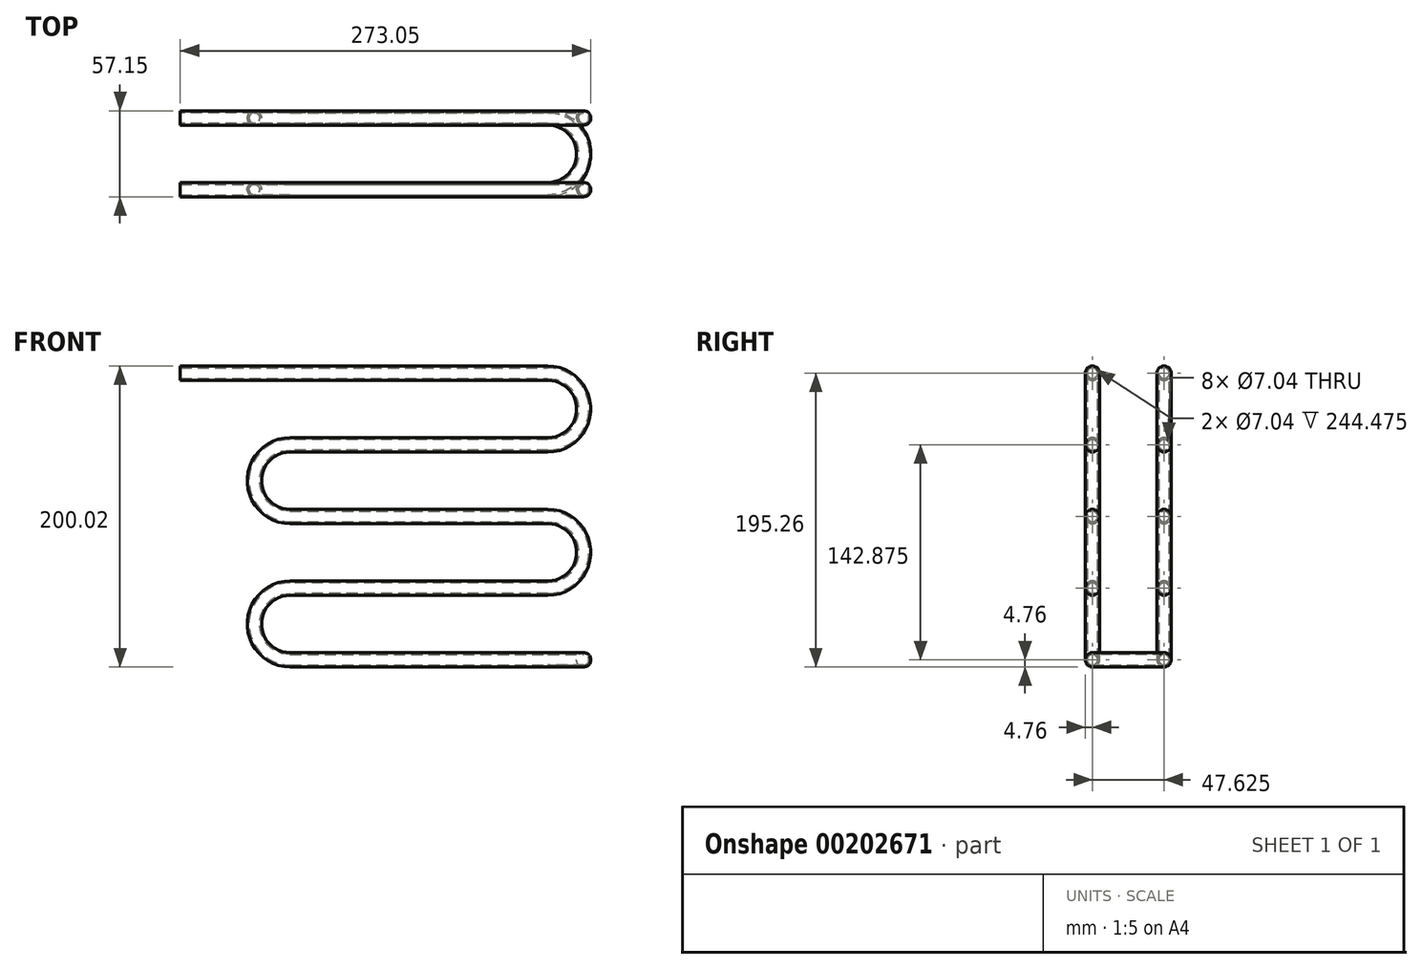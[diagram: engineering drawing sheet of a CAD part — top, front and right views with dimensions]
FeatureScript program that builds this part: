
annotation { "Feature Type Name" : "Feature", "Feature Type Description" : "" }
export const myFeature = defineFeature(function(context is Context, id is Id, definition is map)
    precondition{}
    {
        {
            var Q0;
            Q0=qCreatedBy(makeId("Front.planeOp"),FACE);
            var sketch = newSketch(context, id + "F0", { "sketchPlane" : qUnion([Q0])});
            skLineSegment(sketch, "E0", {"start": v(-55.73, 0) * mm, "end": v(115.72, 0) * mm});
            skArc(sketch, "E1", {"start": v(115.72, -47.63) * mm, "mid": v(139.53, -23.81) * mm, "end": v(115.72, 0) * mm});
            skLineSegment(sketch, "E2", {"start": v(115.72, -47.63) * mm, "end": v(-55.73, -47.63) * mm});
            skArc(sketch, "E3", {"start": v(-55.73, -47.63) * mm, "mid": v(-79.55, -71.44) * mm, "end": v(-55.73, -95.25) * mm});
            skLineSegment(sketch, "E4", {"start": v(-55.73, -95.25) * mm, "end": v(115.72, -95.25) * mm});
            skArc(sketch, "E5", {"start": v(115.72, -142.88) * mm, "mid": v(139.53, -119.06) * mm, "end": v(115.72, -95.25) * mm});
            skLineSegment(sketch, "E6", {"start": v(115.72, -142.88) * mm, "end": v(-55.73, -142.88) * mm});
            skArc(sketch, "E7", {"start": v(-55.73, -142.88) * mm, "mid": v(-79.55, -166.69) * mm, "end": v(-55.73, -190.5) * mm});
            skLineSegment(sketch, "E8", {"start": v(-55.73, -190.5) * mm, "end": v(115.72, -190.5) * mm});
            skSolve(sketch);
        }
        {
            var Q0;
            Q0=qCreatedBy(makeId("Right.planeOp"),FACE);
            var Q1;
            Q1=sQuery(id+"F0.wireOp",VERTEX,"E0.start");
            cPlane(context, id + "F1", {"entities" : qUnion([Q0, Q1]), "cplaneType" : CPlaneType.PLANE_POINT, "offset" : 25.4 * mm, "width" : 152.4 * mm, "height" : 152.4 * mm});
        }
        {
            var Q0;
            Q0=qCreatedBy(id+"F1.planeOp",FACE);
            var sketch = newSketch(context, id + "F2", { "sketchPlane" : qUnion([Q0])});
            skCircle(sketch, "E9", {"center": v(0, 0) * mm, "radius": 4.76 * mm});
            skCircle(sketch, "E10", {"center": v(0, 0) * mm, "radius": 3.52 * mm});
            skSolve(sketch);
        }
        {
            var Q0;
            Q0 = qSketchRegion(id + "F2", true);
            var Q1;
            Q1 = qConstructionFilter(qBodyType(qCreatedBy(id + "F0" ,EDGE), BodyType.WIRE), ConstructionObject.NO);
            sweep(context, id + "F3", {"profiles" : qUnion([Q0]), "path" : qUnion([Q1])});
        }
        {
            var Q0;
            Q0=qCreatedBy(makeId("Top.planeOp"),FACE);
            cPlane(context, id + "F4", {"entities" : qUnion([Q0]), "cplaneType" : CPlaneType.OFFSET, "offset" : 190.5 * mm, "oppositeDirection" : true, "width" : 152.4 * mm, "height" : 152.4 * mm});
        }
        {
            var Q0;
            Q0=qCreatedBy(id+"F4.planeOp",FACE);
            var sketch = newSketch(context, id + "F5", { "sketchPlane" : qUnion([Q0])});
            skArc(sketch, "E11", {"start": v(115.72, 0) * mm, "mid": v(139.53, 23.81) * mm, "end": v(115.72, 47.63) * mm});
            skSolve(sketch);
        }
        {
            var Q0;
            Q0=makeQuery(id+"F3.opSweep","CAP_FACE",FACE,{"disambiguationData":[OSD([sQuery(id+"F0.wireOp",VERTEX,"E8.end"),sQuery(id+"F2.wireOp",EDGE,"E9")])],"isStart":false});
            var sketch = newSketch(context, id + "F6", { "sketchPlane" : qUnion([Q0])});
            skCircle(sketch, "E12", {"center": v(0, -190.5) * mm, "radius": 4.76 * mm});
            skCircle(sketch, "E13", {"center": v(0, -190.5) * mm, "radius": 3.52 * mm});
            skSolve(sketch);
        }
        {
            var Q0;
            Q0 = qSketchRegion(id + "F6", true);
            var Q1;
            Q1 = qConstructionFilter(qBodyType(qCreatedBy(id + "F5" ,EDGE), BodyType.WIRE), ConstructionObject.NO);
            sweep(context, id + "F7", {"operationType" : NewBodyOperationType.ADD, "profiles" : qUnion([Q0]), "path" : qUnion([Q1])});
        }
        {
            var Q0;
            Q0=qCreatedBy(makeId("Front.planeOp"),FACE);
            cPlane(context, id + "F8", {"entities" : qUnion([Q0]), "cplaneType" : CPlaneType.OFFSET, "offset" : 47.62 * mm, "oppositeDirection" : true, "width" : 152.4 * mm, "height" : 152.4 * mm});
        }
        {
            var Q0;
            Q0=qCreatedBy(id+"F8.planeOp",FACE);
            var sketch = newSketch(context, id + "F9", { "sketchPlane" : qUnion([Q0])});
            skLineSegment(sketch, "E14", {"start": v(115.72, -190.5) * mm, "end": v(-55.73, -190.5) * mm});
            skArc(sketch, "E15", {"start": v(-55.73, -142.88) * mm, "mid": v(-79.55, -166.69) * mm, "end": v(-55.73, -190.5) * mm});
            skLineSegment(sketch, "E16", {"start": v(-55.73, -142.87) * mm, "end": v(115.72, -142.87) * mm});
            skArc(sketch, "E17", {"start": v(115.72, -142.88) * mm, "mid": v(139.53, -119.06) * mm, "end": v(115.72, -95.25) * mm});
            skLineSegment(sketch, "E18", {"start": v(115.72, -95.25) * mm, "end": v(-55.73, -95.25) * mm});
            skArc(sketch, "E19", {"start": v(-55.73, -47.62) * mm, "mid": v(-79.55, -71.44) * mm, "end": v(-55.73, -95.25) * mm});
            skLineSegment(sketch, "E20", {"start": v(-55.73, -47.62) * mm, "end": v(115.72, -47.62) * mm});
            skArc(sketch, "E21", {"start": v(115.72, -47.63) * mm, "mid": v(139.53, -23.81) * mm, "end": v(115.72, 0) * mm});
            skLineSegment(sketch, "E22", {"start": v(115.72, 0) * mm, "end": v(-55.73, 0) * mm});
            skSolve(sketch);
        }
        {
            var Q0;
            Q0=makeQuery(id+"F7.opSweep","CAP_FACE",FACE,{"disambiguationData":[OSD([sQuery(id+"F5.wireOp",VERTEX,"E11.end"),sQuery(id+"F6.wireOp",EDGE,"E12")])],"isStart":false});
            var sketch = newSketch(context, id + "F10", { "sketchPlane" : qUnion([Q0])});
            skCircle(sketch, "E23", {"center": v(-47.62, -190.5) * mm, "radius": 4.76 * mm});
            skCircle(sketch, "E24", {"center": v(-47.62, -190.5) * mm, "radius": 3.52 * mm});
            skSolve(sketch);
        }
        {
            var Q0;
            Q0 = qSketchRegion(id + "F10", true);
            var Q1;
            Q1 = qConstructionFilter(qBodyType(qCreatedBy(id + "F9" ,EDGE), BodyType.WIRE), ConstructionObject.NO);
            sweep(context, id + "F11", {"operationType" : NewBodyOperationType.ADD, "profiles" : qUnion([Q0]), "path" : qUnion([Q1])});
        }
        {
            var Q0;
            Q0=makeQuery(id+"F11.opSweep","CAP_FACE",FACE,{"disambiguationData":[OSD([sQuery(id+"F9.wireOp",VERTEX,"E22.end"),sQuery(id+"F10.wireOp",EDGE,"E23")])],"isStart":false});
            var sketch = newSketch(context, id + "F12", { "sketchPlane" : qUnion([Q0])});
            skCircle(sketch, "E25", {"center": v(-47.62, 0) * mm, "radius": 4.76 * mm});
            skCircle(sketch, "E26", {"center": v(0, 0) * mm, "radius": 4.76 * mm});
            skCircle(sketch, "E27", {"center": v(-47.62, 0) * mm, "radius": 3.52 * mm});
            skCircle(sketch, "E28", {"center": v(0, 0) * mm, "radius": 3.52 * mm});
            skSolve(sketch);
        }
        {
            var Q0;
            Q0 = qSketchRegion(id + "F12", true);
            extrude(context, id + "F13", {"entities" : qUnion([Q0]), "operationType" : NewBodyOperationType.ADD, "depth" : 73.02 * mm});
        }
    });
